# Revit family: Unterlegscheibe, zn, 10,5x35x3
name_source: partatom
category: HLS-Bauteile
units: mm (PartAtom-declared; Revit-internal decimal feet)

## family parameters
Arbeitsebenenbasiert = Ja
Beim Laden mit Abzugskörper schneiden = Nein
Bemaßung runder Anschluss = Durchmesser verwenden
Beschriftungsausrichtung beibehalten = Nein
Gemeinsam genutzt = Ja
Immer vertikal = Nein
Raumberechnungspunkt = Nein
Teiletyp = Normal

## types (1)
- Unterlegscheibe, verstärkt 10,5x35x3,0, zn.
    Abmessung = 13 x 37 x 3 mm
    Artikelnummer = 4351053/zn
    Ausführung = verstärkt
    Außendurchmesser = 35 mm  [stored 0.114829 ft]
    D = 35 mm  [stored 0.114829 ft]
    D0 = 11 mm
    EAN = 4250928457172
    Fabrikat = MEFA
    Gewicht = 0.02 kg
    Gewicht pro Bauteil = 0.02 kg
    Innendurchmesser = 11 mm
    Kurztext1 = Unterlegscheibe
    Kurztext2 = 10,5 x 35 x 3 mm ZnNi
    Länge = 3 mm  [stored 0.00984252 ft]
    Material = Stahl
    Mengeneinheit = St
    Oberflaeche = feuerverzinkt
    Stärke = 3 mm  [stored 0.00984252 ft]
    Vorgabe-Ansicht = 1219 mm
    vpe = 100

note: [stored X ft] marks values corroborated as IEEE doubles in the binary element streams (Revit-internal decimal feet)
